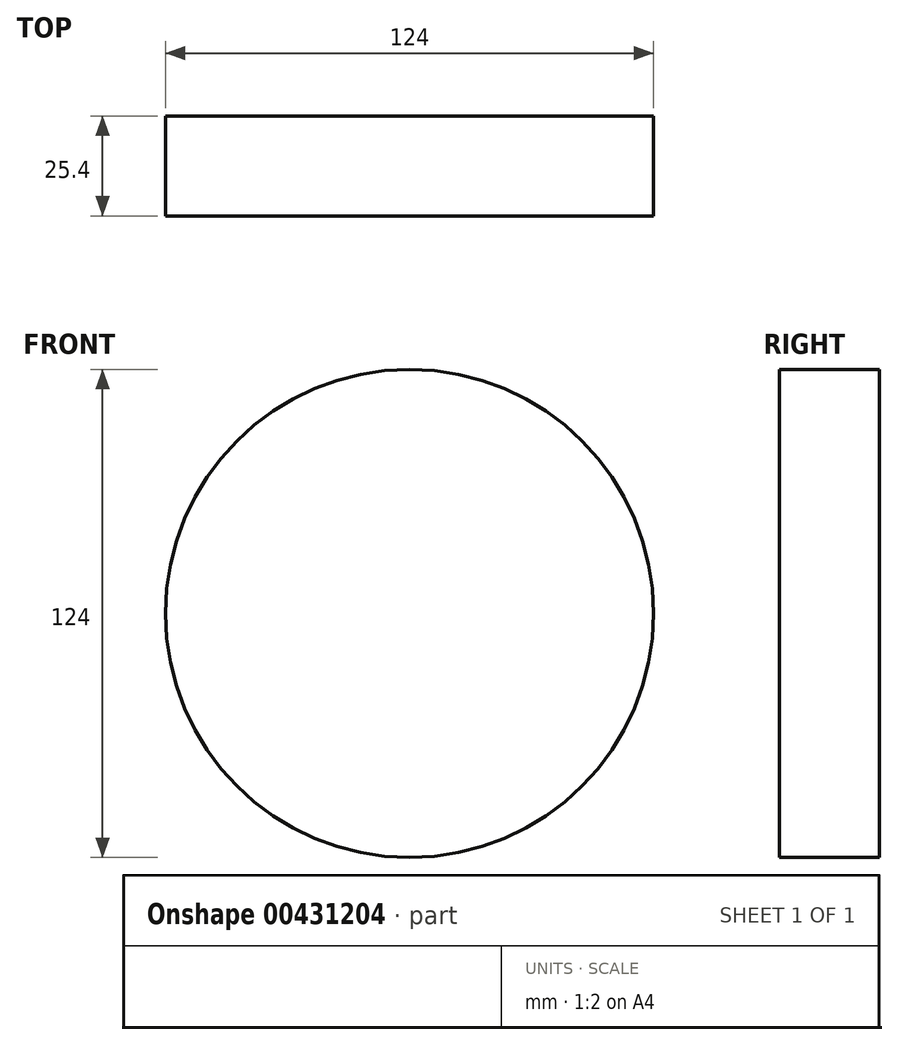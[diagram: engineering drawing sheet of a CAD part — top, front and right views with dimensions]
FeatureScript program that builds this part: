
annotation { "Feature Type Name" : "Feature", "Feature Type Description" : "" }
export const myFeature = defineFeature(function(context is Context, id is Id, definition is map)
    precondition{}
    {
        {
            var Q0;
            Q0=qCreatedBy(makeId("Front.planeOp"),FACE);
            var sketch = newSketch(context, id + "F0", { "sketchPlane" : qUnion([Q0])});
            skCircle(sketch, "E0", {"center": v(0, 0) * mm, "radius": 62 * mm});
            skSolve(sketch);
        }
        {
            var Q0;
            Q0=makeQuery(id+"F0.imprint","IMPRINT",FACE,{"disambiguationData":[TD([[makeQuery(id+"F0.imprint","IMPRINT",EDGE,{"derivedFrom":sQuery(id+"F0.wireOp",EDGE,"E0")}),1.0]])]});
            extrude(context, id + "F1", {"entities" : qUnion([Q0]), "depth" : 25.4 * mm});
        }
    });
